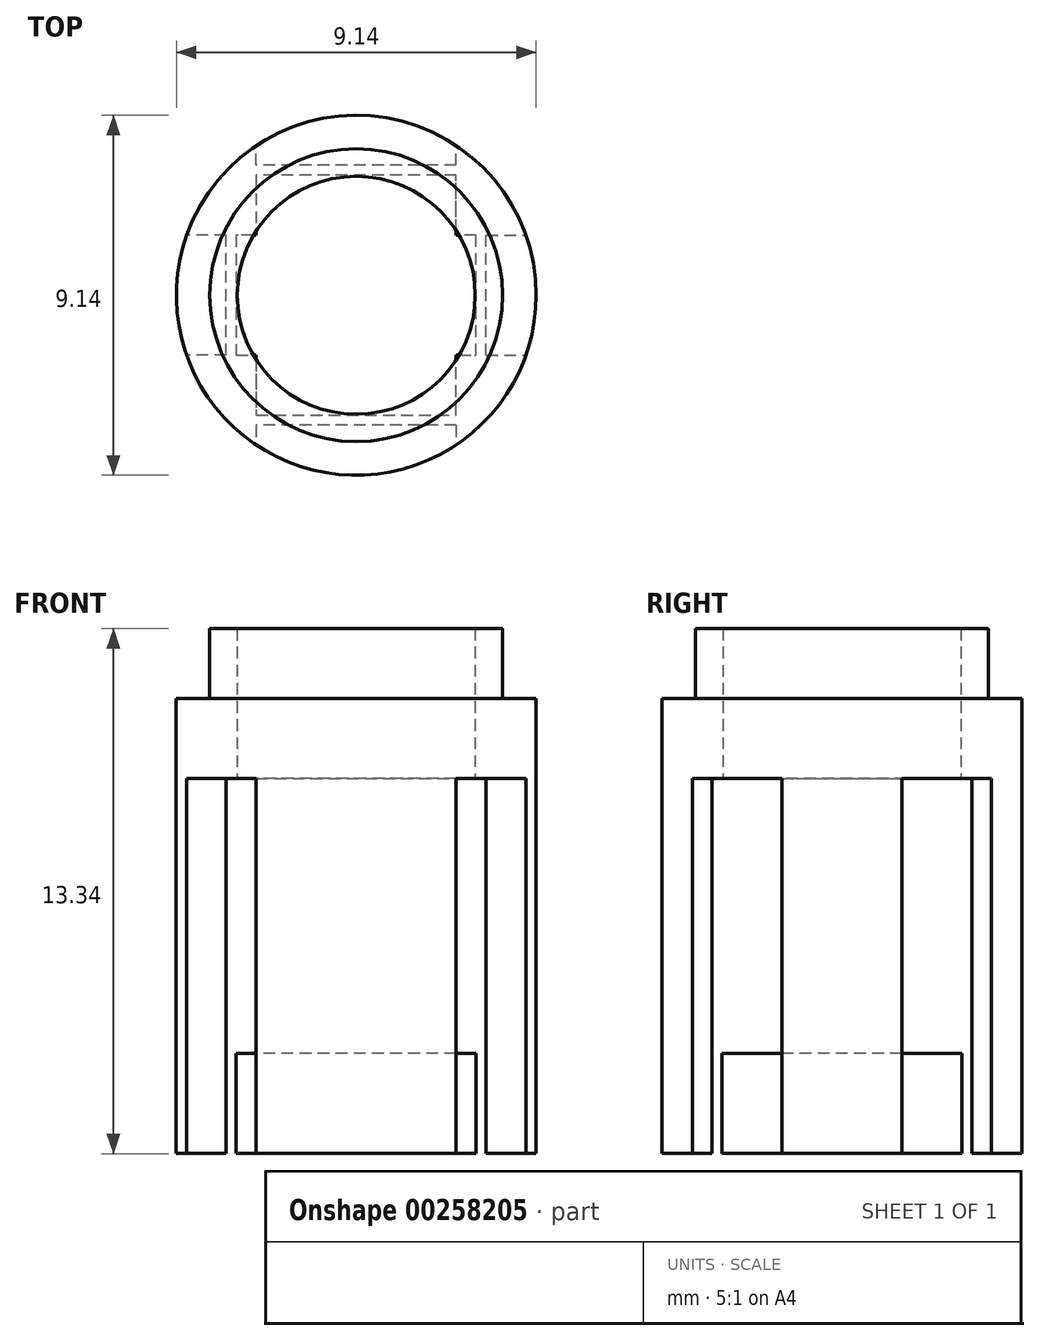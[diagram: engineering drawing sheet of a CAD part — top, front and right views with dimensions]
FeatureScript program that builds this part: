
annotation { "Feature Type Name" : "Feature", "Feature Type Description" : "" }
export const myFeature = defineFeature(function(context is Context, id is Id, definition is map)
    precondition{}
    {
        {
            var Q0;
            Q0=qCreatedBy(makeId("Top.planeOp"),FACE);
            var sketch = newSketch(context, id + "F0", { "sketchPlane" : qUnion([Q0])});
            skCircle(sketch, "E0", {"center": v(0, 0) * mm, "radius": 4.57 * mm});
            skCircle(sketch, "E1", {"center": v(0, 0) * mm, "radius": 3.02 * mm});
            skSolve(sketch);
        }
        {
            var Q0;
            Q0=qSketchRegion(id+"F0",true);
            extrude(context, id + "F1", {"entities" : qUnion([Q0]), "depth" : 3.8 * mm});
        }
        {
            var Q0;
            Q0=makeQuery(id+"F1.opExtrude","CAP_FACE",FACE,{"disambiguationData":[OSD([sQuery(id+"F0.wireOp",EDGE,"E0"),sQuery(id+"F0.wireOp",EDGE,"E1")])],"isStart":false});
            var sketch = newSketch(context, id + "F2", { "sketchPlane" : qUnion([Q0])});
            skCircle(sketch, "E2.0", {"center": v(0, 0) * mm, "radius": 4.57 * mm});
            skCircle(sketch, "E3", {"center": v(0, 0) * mm, "radius": 3.72 * mm});
            skSolve(sketch);
        }
        {
            var Q0;
            Q0=qSketchRegion(id+"F2",true);
            extrude(context, id + "F3", {"entities" : qUnion([Q0]), "operationType" : NewBodyOperationType.REMOVE, "oppositeDirection" : true, "depth" : 1.78 * mm});
        }
        {
            var Q0;
            Q0=makeQuery(id+"F1.opExtrude","CAP_FACE",FACE,{"disambiguationData":[OSD([sQuery(id+"F0.wireOp",EDGE,"E0"),sQuery(id+"F0.wireOp",EDGE,"E1")])],"isStart":true});
            var sketch = newSketch(context, id + "F4", { "sketchPlane" : qUnion([Q0])});
            skCircle(sketch, "E4.0", {"center": v(0, 0) * mm, "radius": 3.02 * mm, "construction": true});
            skArc(sketch, "E5.0", {"start": v(-4.31, 1.52) * mm, "mid": v(-4.57, 0) * mm, "end": v(-4.31, -1.52) * mm});
            skLineSegment(sketch, "E6.bottom", {"start": v(-3.3, 3.3) * mm, "end": v(3.3, 3.3) * mm, "construction": true});
            skLineSegment(sketch, "E6.top", {"start": v(-3.3, -3.3) * mm, "end": v(3.3, -3.3) * mm, "construction": true});
            skLineSegment(sketch, "E6.left", {"start": v(-3.3, 3.3) * mm, "end": v(-3.3, -3.3) * mm, "construction": true});
            skLineSegment(sketch, "E6.right", {"start": v(3.3, 3.3) * mm, "end": v(3.3, -3.3) * mm, "construction": true});
            skPoint(sketch, "E7.positionSnap0", {"position": v(-3.3, 0) * mm});
            skPoint(sketch, "E7.positionSnap1", {"position": v(0, 3.3) * mm});
            skLineSegment(sketch, "E8.bottom", {"start": v(-3.3, 1.52) * mm, "end": v(-4.31, 1.52) * mm});
            skLineSegment(sketch, "E8.top", {"start": v(-3.3, -1.52) * mm, "end": v(-4.31, -1.52) * mm});
            skLineSegment(sketch, "E8.left", {"start": v(-3.3, 1.52) * mm, "end": v(-3.3, -1.52) * mm});
            skLineSegment(sketch, "E9.bottom", {"start": v(2.54, 3.3) * mm, "end": v(2.54, 3.8) * mm});
            skLineSegment(sketch, "E9.top", {"start": v(-2.54, 3.3) * mm, "end": v(-2.54, 3.8) * mm});
            skLineSegment(sketch, "E9.left", {"start": v(2.54, 3.3) * mm, "end": v(-2.54, 3.3) * mm});
            skArc(sketch, "E10.trimOffspring", {"start": v(2.54, 3.8) * mm, "mid": v(0, 4.57) * mm, "end": v(-2.54, 3.8) * mm});
            skLineSegment(sketch, "E11", {"start": v(0, 0) * mm, "end": v(-3.3, 0) * mm, "construction": true});
            skLineSegment(sketch, "E12", {"start": v(0, 0) * mm, "end": v(0, 3.3) * mm, "construction": true});
            skPoint(sketch, "E13.MirrorP", {"position": v(3.3, 0) * mm});
            skLineSegment(sketch, "E14.MirrorCS", {"start": v(3.3, 1.52) * mm, "end": v(4.31, 1.52) * mm});
            skLineSegment(sketch, "E15.MirrorCS", {"start": v(3.3, -1.52) * mm, "end": v(4.31, -1.52) * mm});
            skArc(sketch, "E16.MirrorCS", {"start": v(4.31, 1.52) * mm, "mid": v(4.57, 0) * mm, "end": v(4.31, -1.52) * mm});
            skLineSegment(sketch, "E17.MirrorCS", {"start": v(3.3, 1.52) * mm, "end": v(3.3, -1.52) * mm});
            skPoint(sketch, "E18.MirrorP", {"position": v(0, -3.3) * mm});
            skLineSegment(sketch, "E19.MirrorCS", {"start": v(2.54, -3.3) * mm, "end": v(2.54, -3.8) * mm});
            skLineSegment(sketch, "E20.MirrorCS", {"start": v(2.54, -3.3) * mm, "end": v(-2.54, -3.3) * mm});
            skLineSegment(sketch, "E21.MirrorCS", {"start": v(-2.54, -3.3) * mm, "end": v(-2.54, -3.8) * mm});
            skArc(sketch, "E22.MirrorCS", {"start": v(2.54, -3.8) * mm, "mid": v(0, -4.57) * mm, "end": v(-2.54, -3.8) * mm});
            skSolve(sketch);
        }
        {
            var Q0;
            Q0=qSketchRegion(id+"F4",true);
            extrude(context, id + "F5", {"entities" : qUnion([Q0]), "operationType" : NewBodyOperationType.ADD, "depth" : 6.35 * mm});
        }
        {
            var Q0;
            Q0=makeQuery(id+"F5.opExtrude","CAP_FACE",FACE,{"disambiguationData":[OSD([sQuery(id+"F4.wireOp",EDGE,"E19.MirrorCS"),sQuery(id+"F4.wireOp",EDGE,"E20.MirrorCS"),sQuery(id+"F4.wireOp",EDGE,"E21.MirrorCS"),sQuery(id+"F4.wireOp",EDGE,"E22.MirrorCS")])],"isStart":false});
            var Q1;
            Q1=makeQuery(id+"F5.opExtrude","CAP_FACE",FACE,{"disambiguationData":[OSD([sQuery(id+"F4.wireOp",EDGE,"E9.bottom"),sQuery(id+"F4.wireOp",EDGE,"E9.top"),sQuery(id+"F4.wireOp",EDGE,"E9.left"),sQuery(id+"F4.wireOp",EDGE,"E10.trimOffspring")])],"isStart":false});
            var Q2;
            Q2=makeQuery(id+"F5.opExtrude","CAP_FACE",FACE,{"disambiguationData":[OSD([sQuery(id+"F4.wireOp",EDGE,"E5.0"),sQuery(id+"F4.wireOp",EDGE,"E8.bottom"),sQuery(id+"F4.wireOp",EDGE,"E8.top"),sQuery(id+"F4.wireOp",EDGE,"E8.left")])],"isStart":false});
            var Q3;
            Q3=makeQuery(id+"F5.opExtrude","CAP_FACE",FACE,{"disambiguationData":[OSD([sQuery(id+"F4.wireOp",EDGE,"E14.MirrorCS"),sQuery(id+"F4.wireOp",EDGE,"E15.MirrorCS"),sQuery(id+"F4.wireOp",EDGE,"E16.MirrorCS"),sQuery(id+"F4.wireOp",EDGE,"E17.MirrorCS")])],"isStart":false});
            extrude(context, id + "F6", {"entities" : qUnion([Q0, Q1, Q2, Q3]), "operationType" : NewBodyOperationType.ADD, "depth" : 3.17 * mm});
        }
        {
            var Q0;
            Q0=makeQuery(id+"F6.opExtrude","CAP_FACE",FACE,{"disambiguationData":[OSD([sQuery(id+"F4.wireOp",EDGE,"E14.MirrorCS"),sQuery(id+"F4.wireOp",EDGE,"E15.MirrorCS"),sQuery(id+"F4.wireOp",EDGE,"E16.MirrorCS"),sQuery(id+"F4.wireOp",EDGE,"E17.MirrorCS")])],"isStart":false});
            var sketch = newSketch(context, id + "F7", { "sketchPlane" : qUnion([Q0])});
            skPoint(sketch, "E23.0", {"position": v(0, 3.3) * mm});
            skLineSegment(sketch, "E24.0", {"start": v(2.54, -3.3) * mm, "end": v(-2.54, -3.3) * mm, "construction": true});
            skPoint(sketch, "E25.0", {"position": v(-3.3, 0) * mm});
            skPoint(sketch, "E26.0", {"position": v(3.3, 0) * mm});
            skLineSegment(sketch, "E27", {"start": v(-3.3, 0) * mm, "end": v(3.3, 0) * mm, "construction": true});
            skLineSegment(sketch, "E28.bottom", {"start": v(-3.05, 3.05) * mm, "end": v(3.05, 3.05) * mm, "construction": true});
            skLineSegment(sketch, "E28.top", {"start": v(-3.05, -3.05) * mm, "end": v(3.05, -3.05) * mm, "construction": true});
            skLineSegment(sketch, "E28.left", {"start": v(-3.05, 3.05) * mm, "end": v(-3.05, -3.05) * mm, "construction": true});
            skLineSegment(sketch, "E28.right", {"start": v(3.05, 3.05) * mm, "end": v(3.05, -3.05) * mm, "construction": true});
            skPoint(sketch, "E29", {"position": v(0, 0) * mm});
            skPoint(sketch, "E29.positionSnap0", {"position": v(-3.05, 0) * mm});
            skPoint(sketch, "E29.positionSnap1", {"position": v(0, 3.05) * mm});
            skPoint(sketch, "E30.0", {"position": v(-3.3, 1.52) * mm});
            skPoint(sketch, "E31.0", {"position": v(-3.3, -1.52) * mm});
            skPoint(sketch, "E32.0", {"position": v(-2.54, 3.3) * mm});
            skPoint(sketch, "E33.0", {"position": v(2.54, 3.3) * mm});
            skPoint(sketch, "E34.0", {"position": v(3.3, -1.52) * mm});
            skPoint(sketch, "E35.0", {"position": v(3.3, 1.52) * mm});
            skLineSegment(sketch, "E36", {"start": v(-2.54, 3.3) * mm, "end": v(-2.54, -3.3) * mm, "construction": true});
            skLineSegment(sketch, "E37", {"start": v(2.54, 3.3) * mm, "end": v(2.54, -3.3) * mm, "construction": true});
            skLineSegment(sketch, "E38", {"start": v(3.3, -1.52) * mm, "end": v(-3.3, -1.52) * mm, "construction": true});
            skLineSegment(sketch, "E39", {"start": v(-3.3, 1.52) * mm, "end": v(3.3, 1.52) * mm, "construction": true});
            skLineSegment(sketch, "E40", {"start": v(-3.05, 1.52) * mm, "end": v(-2.54, 1.52) * mm});
            skLineSegment(sketch, "E41", {"start": v(-2.54, 1.52) * mm, "end": v(-2.54, 3.05) * mm});
            skLineSegment(sketch, "E42", {"start": v(-2.54, 3.05) * mm, "end": v(2.54, 3.05) * mm});
            skLineSegment(sketch, "E43", {"start": v(2.54, 3.05) * mm, "end": v(2.54, 1.52) * mm});
            skLineSegment(sketch, "E44", {"start": v(2.54, 1.52) * mm, "end": v(3.05, 1.52) * mm});
            skLineSegment(sketch, "E45", {"start": v(3.05, 1.52) * mm, "end": v(3.05, -1.52) * mm});
            skLineSegment(sketch, "E46", {"start": v(3.05, -1.52) * mm, "end": v(2.54, -1.52) * mm});
            skLineSegment(sketch, "E47", {"start": v(2.54, -1.52) * mm, "end": v(2.54, -3.05) * mm});
            skLineSegment(sketch, "E48", {"start": v(2.54, -3.05) * mm, "end": v(-2.54, -3.05) * mm});
            skLineSegment(sketch, "E49", {"start": v(-2.54, -3.05) * mm, "end": v(-2.54, -1.52) * mm});
            skLineSegment(sketch, "E50", {"start": v(-2.54, -1.52) * mm, "end": v(-3.05, -1.52) * mm});
            skLineSegment(sketch, "E51", {"start": v(-3.05, -1.52) * mm, "end": v(-3.05, 1.52) * mm});
            skSolve(sketch);
        }
        {
            var Q0;
            Q0=qSketchRegion(id+"F7",true);
            extrude(context, id + "F8", {"entities" : qUnion([Q0]), "oppositeDirection" : true, "depth" : 2.54 * mm});
        }
        {
            var Q0;
            Q0=qCreatedBy(makeId("Top.planeOp"),FACE);
            cPlane(context, id + "F9", {"entities" : qUnion([Q0]), "cplaneType" : CPlaneType.OFFSET, "offset" : 25.4 * mm, "oppositeDirection" : true, "width" : 152.4 * mm, "height" : 152.4 * mm});
        }
        {
            var Q0;
            Q0=qCreatedBy(id+"F9.planeOp",FACE);
            var sketch = newSketch(context, id + "F10", { "sketchPlane" : qUnion([Q0])});
            skArc(sketch, "E52", {"start": v(-4.04, 3.82) * mm, "mid": v(-5.56, 0) * mm, "end": v(-4.04, -3.82) * mm});
            skLineSegment(sketch, "E53", {"start": v(0, 0) * mm, "end": v(0, 6.2) * mm, "construction": true});
            skLineSegment(sketch, "E54", {"start": v(0, 0) * mm, "end": v(-6.03, 0) * mm, "construction": true});
            skLineSegment(sketch, "E55.bottom", {"start": v(5.32, 1.59) * mm, "end": v(10.38, 1.59) * mm});
            skLineSegment(sketch, "E55.top", {"start": v(5.32, -1.59) * mm, "end": v(10.38, -1.59) * mm});
            skLineSegment(sketch, "E55.right", {"start": v(10.38, 1.59) * mm, "end": v(10.38, -1.59) * mm});
            skPoint(sketch, "E56", {"position": v(5.3, 0) * mm});
            skLineSegment(sketch, "E57.1.0", {"start": v(-1.29, 5.4) * mm, "end": v(-3.82, 9.79) * mm});
            skLineSegment(sketch, "E57.1.1", {"start": v(-6.57, 8.2) * mm, "end": v(-3.82, 9.79) * mm});
            skLineSegment(sketch, "E57.1.2", {"start": v(-4.04, 3.82) * mm, "end": v(-6.57, 8.2) * mm});
            skLineSegment(sketch, "E57.2.0", {"start": v(-4.04, -3.82) * mm, "end": v(-6.57, -8.2) * mm});
            skLineSegment(sketch, "E57.2.1", {"start": v(-3.82, -9.79) * mm, "end": v(-6.57, -8.2) * mm});
            skLineSegment(sketch, "E57.2.2", {"start": v(-1.29, -5.4) * mm, "end": v(-3.82, -9.79) * mm});
            skArc(sketch, "E58.trimOffspring", {"start": v(-1.29, -5.4) * mm, "mid": v(2.78, -4.81) * mm, "end": v(5.32, -1.59) * mm});
            skArc(sketch, "E59.trimOffspring", {"start": v(5.32, 1.59) * mm, "mid": v(2.78, 4.81) * mm, "end": v(-1.29, 5.4) * mm});
            skPoint(sketch, "E60.orphan", {"position": v(5.3, 1.59) * mm});
            skPoint(sketch, "E61.orphan", {"position": v(5.3, -1.59) * mm});
            skPoint(sketch, "E62.orphan", {"position": v(-4.03, -3.8) * mm});
            skPoint(sketch, "E63.orphan", {"position": v(-1.28, -5.39) * mm});
            skPoint(sketch, "E64.orphan", {"position": v(-1.28, 5.39) * mm});
            skPoint(sketch, "E65.orphan", {"position": v(-4.03, 3.8) * mm});
            skLineSegment(sketch, "E66.0", {"start": v(-2.8, 1.78) * mm, "end": v(-2.8, -1.78) * mm});
            skLineSegment(sketch, "E67.0", {"start": v(-2.8, 1.78) * mm, "end": v(-4.49, 1.78) * mm});
            skLineSegment(sketch, "E68.0", {"start": v(-2.8, -1.78) * mm, "end": v(-4.49, -1.78) * mm});
            skArc(sketch, "E69", {"start": v(-2.8, -3.93) * mm, "mid": v(0, -4.82) * mm, "end": v(2.8, -3.93) * mm});
            skLineSegment(sketch, "E70.0", {"start": v(-2.8, -2.8) * mm, "end": v(-2.8, -3.93) * mm});
            skLineSegment(sketch, "E71.0", {"start": v(-2.8, -2.8) * mm, "end": v(2.8, -2.8) * mm});
            skLineSegment(sketch, "E72.MirrorCS", {"start": v(-5.59, 0) * mm, "end": v(-5.59, 6.2) * mm, "construction": true});
            skLineSegment(sketch, "E73.MirrorCS", {"start": v(2.8, -2.8) * mm, "end": v(2.8, -3.93) * mm});
            skArc(sketch, "E74.trimOffspring", {"start": v(-4.49, 1.78) * mm, "mid": v(-4.82, 0) * mm, "end": v(-4.49, -1.78) * mm});
            skLineSegment(sketch, "E75.MirrorCS", {"start": v(-2.8, 2.8) * mm, "end": v(2.8, 2.8) * mm});
            skLineSegment(sketch, "E76.MirrorCS", {"start": v(2.8, 2.8) * mm, "end": v(2.8, 3.93) * mm});
            skLineSegment(sketch, "E77.MirrorCS", {"start": v(-2.8, 2.8) * mm, "end": v(-2.8, 3.93) * mm});
            skArc(sketch, "E78.MirrorCS", {"start": v(-2.8, 3.93) * mm, "mid": v(0, 4.82) * mm, "end": v(2.8, 3.93) * mm});
            skLineSegment(sketch, "E79.MirrorCS", {"start": v(2.8, -1.78) * mm, "end": v(4.49, -1.78) * mm});
            skLineSegment(sketch, "E80.MirrorCS", {"start": v(2.8, 1.78) * mm, "end": v(2.8, -1.78) * mm});
            skLineSegment(sketch, "E81.MirrorCS", {"start": v(2.8, 1.78) * mm, "end": v(4.49, 1.78) * mm});
            skArc(sketch, "E82.MirrorCS", {"start": v(4.49, 1.78) * mm, "mid": v(4.82, 0) * mm, "end": v(4.49, -1.78) * mm});
            skSolve(sketch);
        }
        {
            var Q0;
            Q0=qSketchRegion(id+"F10",true);
            extrude(context, id + "F11", {"entities" : qUnion([Q0]), "depth" : 6.35 * mm});
        }
        {
            var Q0;
            Q0=makeQuery(id+"F11.opExtrude","CAP_FACE",FACE,{"disambiguationData":[OSD([sQuery(id+"F10.wireOp",EDGE,"db18d521-57b8-4300-b0c5-4cde51a523bd.0.0"),sQuery(id+"F10.wireOp",EDGE,"db18d521-57b8-4300-b0c5-4cde51a523bd.0.3"),sQuery(id+"F10.wireOp",EDGE,"db18d521-57b8-4300-b0c5-4cde51a523bd.0.6"),sQuery(id+"F10.wireOp",EDGE,"db18d521-57b8-4300-b0c5-4cde51a523bd.0.9"),sQuery(id+"F10.wireOp",EDGE,"369de0dd-4191-417d-bcee-15261e193363.0"),sQuery(id+"F10.wireOp",EDGE,"E52"),sQuery(id+"F10.wireOp",EDGE,"kX5wIPr1-428x-K9z2-gXJk-3hD54hDqaICx"),sQuery(id+"F10.wireOp",EDGE,"egBcWlUM-x16y-42HG-bm2Q-WMoGCDpll3w8"),sQuery(id+"F10.wireOp",EDGE,"77dcda4e-ead9-4f28-8145-114dee90182b0.MirrorCS"),sQuery(id+"F10.wireOp",EDGE,"77dcda4e-ead9-4f28-8145-114dee90182b1.MirrorCS"),sQuery(id+"F10.wireOp",EDGE,"fe240c59-e6ec-4a6d-bc8b-0338589bbb20.trimOffspring"),sQuery(id+"F10.wireOp",EDGE,"713e28b8-72cb-480b-ac16-a4ad6be82ba40.MirrorCS"),sQuery(id+"F10.wireOp",EDGE,"713e28b8-72cb-480b-ac16-a4ad6be82ba41.MirrorCS"),sQuery(id+"F10.wireOp",EDGE,"713e28b8-72cb-480b-ac16-a4ad6be82ba42.MirrorCS"),sQuery(id+"F10.wireOp",EDGE,"713e28b8-72cb-480b-ac16-a4ad6be82ba43.MirrorCS"),sQuery(id+"F10.wireOp",EDGE,"104ba62b-27fc-46a6-bafd-026f3a624c96.trimOffspring"),sQuery(id+"F10.wireOp",EDGE,"f2ccea3b-76f7-4db3-a6ea-49b77455acce.trimOffspring"),sQuery(id+"F10.wireOp",EDGE,"E55.bottom"),sQuery(id+"F10.wireOp",EDGE,"E55.top"),sQuery(id+"F10.wireOp",EDGE,"E55.right"),sQuery(id+"F10.wireOp",EDGE,"E57.1.0"),sQuery(id+"F10.wireOp",EDGE,"E57.1.1"),sQuery(id+"F10.wireOp",EDGE,"E57.1.2"),sQuery(id+"F10.wireOp",EDGE,"E57.2.0"),sQuery(id+"F10.wireOp",EDGE,"E57.2.1"),sQuery(id+"F10.wireOp",EDGE,"E57.2.2"),sQuery(id+"F10.wireOp",EDGE,"E58.trimOffspring"),sQuery(id+"F10.wireOp",EDGE,"E59.trimOffspring")])],"isStart":false});
            var sketch = newSketch(context, id + "F12", { "sketchPlane" : qUnion([Q0])});
            skLineSegment(sketch, "E83.0.0", {"start": v(10.38, 1.59) * mm, "end": v(5.32, 1.59) * mm});
            skArc(sketch, "E83.0.1", {"start": v(5.32, 1.59) * mm, "mid": v(2.78, 4.81) * mm, "end": v(-1.29, 5.4) * mm});
            skLineSegment(sketch, "E83.0.2", {"start": v(-1.29, 5.4) * mm, "end": v(-3.82, 9.79) * mm});
            skLineSegment(sketch, "E83.0.3", {"start": v(-3.82, 9.79) * mm, "end": v(-6.57, 8.2) * mm});
            skLineSegment(sketch, "E83.0.4", {"start": v(-6.57, 8.2) * mm, "end": v(-4.04, 3.82) * mm});
            skArc(sketch, "E83.0.5", {"start": v(-4.04, 3.82) * mm, "mid": v(-5.56, 0) * mm, "end": v(-4.04, -3.82) * mm});
            skLineSegment(sketch, "E83.0.6", {"start": v(-4.04, -3.82) * mm, "end": v(-6.57, -8.2) * mm});
            skLineSegment(sketch, "E83.0.7", {"start": v(-6.57, -8.2) * mm, "end": v(-3.82, -9.79) * mm});
            skLineSegment(sketch, "E83.0.8", {"start": v(-3.82, -9.79) * mm, "end": v(-1.29, -5.4) * mm});
            skArc(sketch, "E83.0.9", {"start": v(-1.29, -5.4) * mm, "mid": v(2.78, -4.81) * mm, "end": v(5.32, -1.59) * mm});
            skLineSegment(sketch, "E83.0.10", {"start": v(5.32, -1.59) * mm, "end": v(10.38, -1.59) * mm});
            skLineSegment(sketch, "E83.0.11", {"start": v(10.38, -1.59) * mm, "end": v(10.38, 1.59) * mm});
            skArc(sketch, "E84.0", {"start": v(-4.49, 1.78) * mm, "mid": v(-4.82, 0) * mm, "end": v(-4.49, -1.78) * mm, "construction": true});
            skArc(sketch, "E85.0", {"start": v(-2.8, 3.93) * mm, "mid": v(0, 4.82) * mm, "end": v(2.8, 3.93) * mm, "construction": true});
            skArc(sketch, "E86.0", {"start": v(4.49, 1.78) * mm, "mid": v(4.82, 0) * mm, "end": v(4.49, -1.78) * mm, "construction": true});
            skArc(sketch, "E87.0", {"start": v(-2.8, -3.93) * mm, "mid": v(0, -4.82) * mm, "end": v(2.8, -3.93) * mm, "construction": true});
            skArc(sketch, "E88", {"start": v(-3.93, -2.8) * mm, "mid": v(0, -4.82) * mm, "end": v(3.93, -2.8) * mm});
            skLineSegment(sketch, "E89.0", {"start": v(-2.8, -2.8) * mm, "end": v(2.8, -2.8) * mm, "construction": true});
            skLineSegment(sketch, "E90.0", {"start": v(-2.8, -1.78) * mm, "end": v(-4.49, -1.78) * mm, "construction": true});
            skLineSegment(sketch, "E91.0", {"start": v(2.8, -1.78) * mm, "end": v(4.49, -1.78) * mm, "construction": true});
            skLineSegment(sketch, "E92.bottom", {"start": v(-4.49, -1.78) * mm, "end": v(4.49, -1.78) * mm});
            skLineSegment(sketch, "E92.top", {"start": v(-3.93, -2.8) * mm, "end": v(3.93, -2.8) * mm});
            skPoint(sketch, "E92.right.end.orphan", {"position": v(4.49, -2.8) * mm});
            skArc(sketch, "E93.trimOffspring", {"start": v(4.49, -1.78) * mm, "mid": v(4.82, 0) * mm, "end": v(4.49, 1.78) * mm});
            skLineSegment(sketch, "E94.0", {"start": v(-2.8, 1.78) * mm, "end": v(-4.49, 1.78) * mm, "construction": true});
            skLineSegment(sketch, "E95.0", {"start": v(-2.8, 2.8) * mm, "end": v(2.8, 2.8) * mm, "construction": true});
            skLineSegment(sketch, "E96.0", {"start": v(2.8, 1.78) * mm, "end": v(4.49, 1.78) * mm, "construction": true});
            skLineSegment(sketch, "E97.bottom", {"start": v(-4.49, 1.78) * mm, "end": v(4.49, 1.78) * mm});
            skLineSegment(sketch, "E97.top", {"start": v(-3.93, 2.8) * mm, "end": v(3.93, 2.8) * mm});
            skArc(sketch, "E98.trimOffspring", {"start": v(-4.49, 1.78) * mm, "mid": v(-4.82, 0) * mm, "end": v(-4.49, -1.78) * mm});
            skPoint(sketch, "E99.orphan", {"position": v(4.49, 2.8) * mm});
            skArc(sketch, "E100.trimOffspring", {"start": v(3.93, 2.8) * mm, "mid": v(0, 4.82) * mm, "end": v(-3.93, 2.8) * mm});
            skSolve(sketch);
        }
        {
            var Q0;
            Q0=qSketchRegion(id+"F12",true);
            extrude(context, id + "F13", {"entities" : qUnion([Q0]), "operationType" : NewBodyOperationType.ADD, "depth" : 3.17 * mm});
        }
        {
            var Q0;
            Q0=makeQuery(id+"F13.opExtrude","CAP_FACE",FACE,{"disambiguationData":[OSD([sQuery(id+"F12.wireOp",EDGE,"E83.0.0"),sQuery(id+"F12.wireOp",EDGE,"E83.0.1"),sQuery(id+"F12.wireOp",EDGE,"E83.0.2"),sQuery(id+"F12.wireOp",EDGE,"E83.0.3"),sQuery(id+"F12.wireOp",EDGE,"E83.0.4"),sQuery(id+"F12.wireOp",EDGE,"E83.0.5"),sQuery(id+"F12.wireOp",EDGE,"E83.0.6"),sQuery(id+"F12.wireOp",EDGE,"E83.0.7"),sQuery(id+"F12.wireOp",EDGE,"E83.0.8"),sQuery(id+"F12.wireOp",EDGE,"E83.0.9"),sQuery(id+"F12.wireOp",EDGE,"E83.0.10"),sQuery(id+"F12.wireOp",EDGE,"E83.0.11"),sQuery(id+"F12.wireOp",EDGE,"E88"),sQuery(id+"F12.wireOp",EDGE,"E92.bottom"),sQuery(id+"F12.wireOp",EDGE,"E92.top"),sQuery(id+"F12.wireOp",EDGE,"E93.trimOffspring"),sQuery(id+"F12.wireOp",EDGE,"E97.bottom"),sQuery(id+"F12.wireOp",EDGE,"E97.top"),sQuery(id+"F12.wireOp",EDGE,"E98.trimOffspring"),sQuery(id+"F12.wireOp",EDGE,"E100.trimOffspring")])],"isStart":false});
            var sketch = newSketch(context, id + "F14", { "sketchPlane" : qUnion([Q0])});
            skLineSegment(sketch, "E101.0.0", {"start": v(10.38, 1.59) * mm, "end": v(5.32, 1.59) * mm});
            skArc(sketch, "E101.0.1", {"start": v(5.32, 1.59) * mm, "mid": v(2.78, 4.81) * mm, "end": v(-1.29, 5.4) * mm});
            skLineSegment(sketch, "E101.0.2", {"start": v(-1.29, 5.4) * mm, "end": v(-3.82, 9.79) * mm});
            skLineSegment(sketch, "E101.0.3", {"start": v(-3.82, 9.79) * mm, "end": v(-6.57, 8.2) * mm});
            skLineSegment(sketch, "E101.0.4", {"start": v(-6.57, 8.2) * mm, "end": v(-4.04, 3.82) * mm});
            skArc(sketch, "E101.0.5", {"start": v(-4.04, 3.82) * mm, "mid": v(-5.56, 0) * mm, "end": v(-4.04, -3.82) * mm});
            skLineSegment(sketch, "E101.0.6", {"start": v(-4.04, -3.82) * mm, "end": v(-6.57, -8.2) * mm});
            skLineSegment(sketch, "E101.0.7", {"start": v(-6.57, -8.2) * mm, "end": v(-3.82, -9.79) * mm});
            skLineSegment(sketch, "E101.0.8", {"start": v(-3.82, -9.79) * mm, "end": v(-1.29, -5.4) * mm});
            skArc(sketch, "E101.0.9", {"start": v(-1.29, -5.4) * mm, "mid": v(2.78, -4.81) * mm, "end": v(5.32, -1.59) * mm});
            skLineSegment(sketch, "E101.0.10", {"start": v(5.32, -1.59) * mm, "end": v(10.38, -1.59) * mm});
            skLineSegment(sketch, "E101.0.11", {"start": v(10.38, -1.59) * mm, "end": v(10.38, 1.59) * mm});
            skCircle(sketch, "E102", {"center": v(0, 0) * mm, "radius": 4.82 * mm});
            skSolve(sketch);
        }
        {
            var Q0;
            Q0=qSketchRegion(id+"F14",true);
            extrude(context, id + "F15", {"entities" : qUnion([Q0]), "operationType" : NewBodyOperationType.ADD, "depth" : 3.17 * mm});
        }
        {
            var Q0;
            Q0=makeQuery(id+"F11.opExtrude","SWEPT_BODY",BODY,{"disambiguationData":[OSD([sQuery(id+"F10.wireOp",EDGE,"E52"),sQuery(id+"F10.wireOp",EDGE,"E55.bottom"),sQuery(id+"F10.wireOp",EDGE,"E55.top"),sQuery(id+"F10.wireOp",EDGE,"E55.right"),sQuery(id+"F10.wireOp",EDGE,"E57.1.0"),sQuery(id+"F10.wireOp",EDGE,"E57.1.1"),sQuery(id+"F10.wireOp",EDGE,"E57.1.2"),sQuery(id+"F10.wireOp",EDGE,"E57.2.0"),sQuery(id+"F10.wireOp",EDGE,"E57.2.1"),sQuery(id+"F10.wireOp",EDGE,"E57.2.2"),sQuery(id+"F10.wireOp",EDGE,"E58.trimOffspring"),sQuery(id+"F10.wireOp",EDGE,"E59.trimOffspring"),sQuery(id+"F10.wireOp",EDGE,"E66.0"),sQuery(id+"F10.wireOp",EDGE,"E67.0"),sQuery(id+"F10.wireOp",EDGE,"E68.0"),sQuery(id+"F10.wireOp",EDGE,"E69"),sQuery(id+"F10.wireOp",EDGE,"E70.0"),sQuery(id+"F10.wireOp",EDGE,"E71.0"),sQuery(id+"F10.wireOp",EDGE,"E73.MirrorCS"),sQuery(id+"F10.wireOp",EDGE,"E74.trimOffspring"),sQuery(id+"F10.wireOp",EDGE,"E75.MirrorCS"),sQuery(id+"F10.wireOp",EDGE,"E76.MirrorCS"),sQuery(id+"F10.wireOp",EDGE,"E77.MirrorCS"),sQuery(id+"F10.wireOp",EDGE,"E78.MirrorCS"),sQuery(id+"F10.wireOp",EDGE,"E79.MirrorCS"),sQuery(id+"F10.wireOp",EDGE,"E80.MirrorCS"),sQuery(id+"F10.wireOp",EDGE,"E81.MirrorCS"),sQuery(id+"F10.wireOp",EDGE,"E82.MirrorCS")])]});
            deleteBodies(context, id + "F16", {"entities" : qUnion([Q0])});
        }
    });
